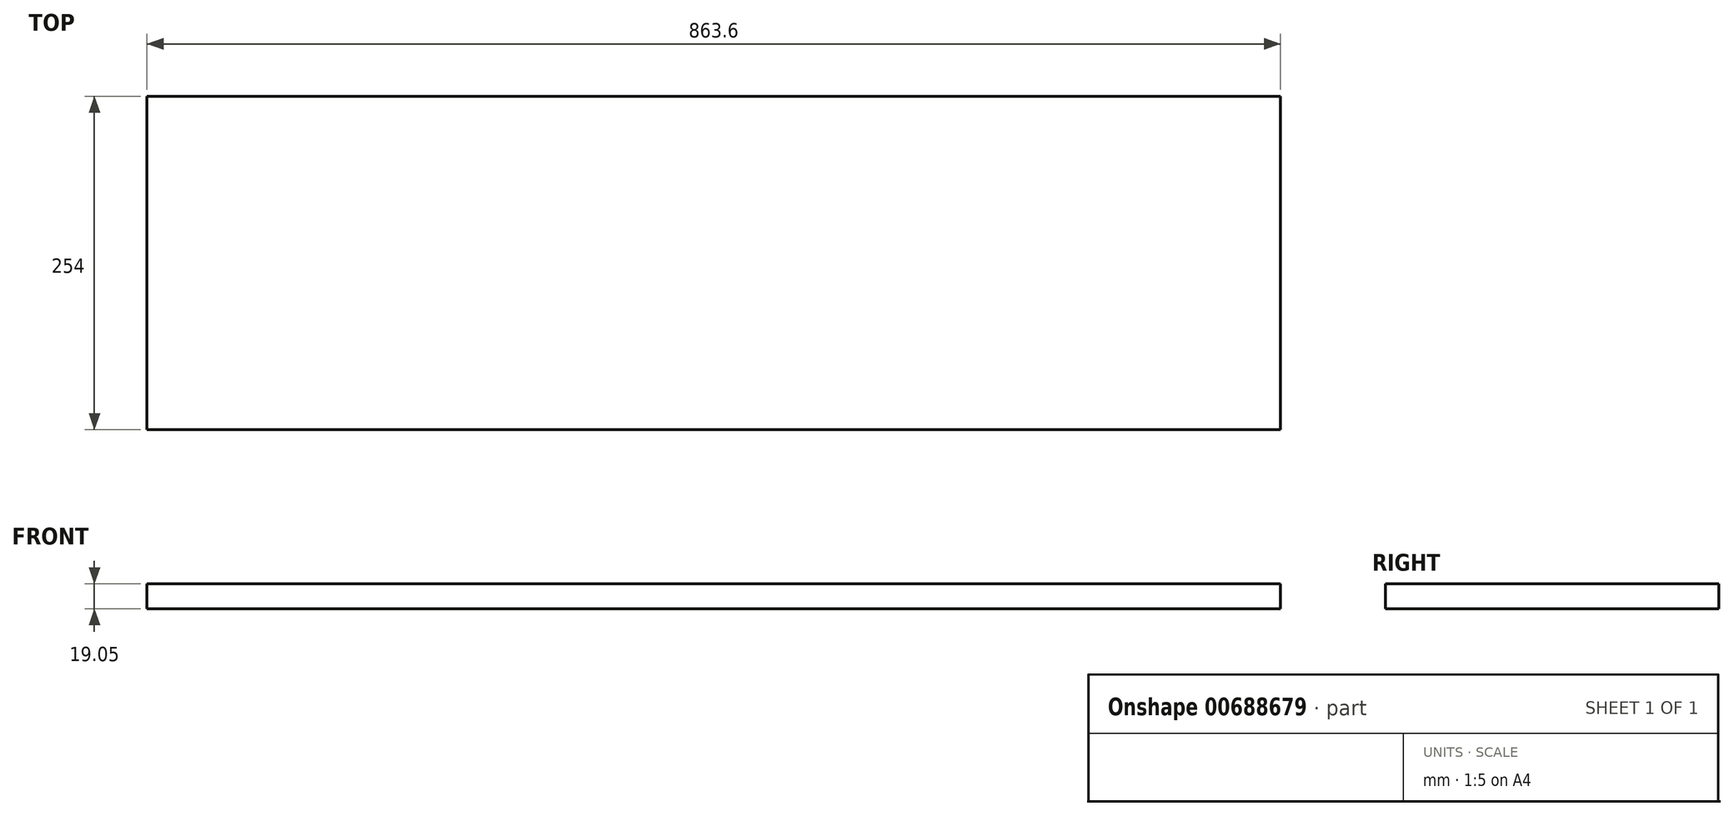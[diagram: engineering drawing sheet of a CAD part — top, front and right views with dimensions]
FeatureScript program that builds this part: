
annotation { "Feature Type Name" : "Feature", "Feature Type Description" : "" }
export const myFeature = defineFeature(function(context is Context, id is Id, definition is map)
    precondition{}
    {
        {
            var Q0;
            Q0=qCreatedBy(makeId("Top.planeOp"),FACE);
            var sketch = newSketch(context, id + "F0", { "sketchPlane" : qUnion([Q0])});
            skLineSegment(sketch, "E0.bottom", {"start": v(431.8, 127) * mm, "end": v(-431.8, 127) * mm});
            skLineSegment(sketch, "E0.top", {"start": v(431.8, -127) * mm, "end": v(-431.8, -127) * mm});
            skLineSegment(sketch, "E0.left", {"start": v(431.8, 127) * mm, "end": v(431.8, -127) * mm});
            skLineSegment(sketch, "E0.right", {"start": v(-431.8, 127) * mm, "end": v(-431.8, -127) * mm});
            skPoint(sketch, "E0.middle", {"position": v(0, 0) * mm});
            skSolve(sketch);
        }
        {
            var Q0;
            Q0=makeQuery(id+"F0.imprint","IMPRINT",FACE,{"disambiguationData":[TD([[makeQuery(id+"F0.imprint","IMPRINT",EDGE,{"derivedFrom":sQuery(id+"F0.wireOp",EDGE,"E0.bottom")}),1.0]])]});
            extrude(context, id + "F1", {"entities" : qUnion([Q0]), "depth" : 19.05 * mm, "offsetDistance" : 25.4 * mm});
        }
    });
